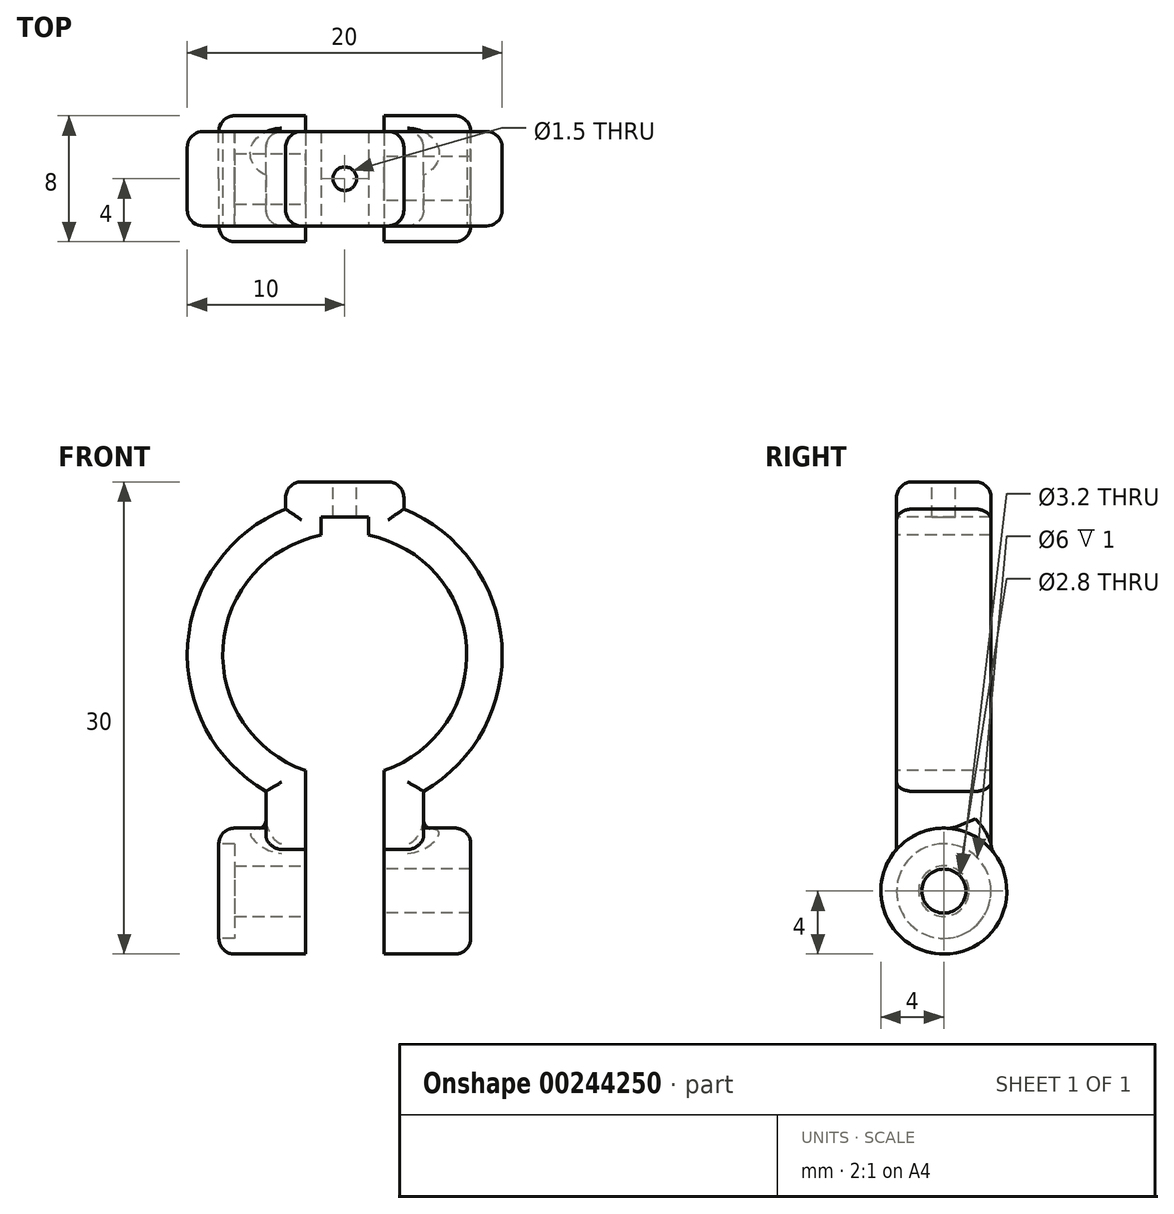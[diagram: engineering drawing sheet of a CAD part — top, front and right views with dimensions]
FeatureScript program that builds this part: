
annotation { "Feature Type Name" : "Feature", "Feature Type Description" : "" }
export const myFeature = defineFeature(function(context is Context, id is Id, definition is map)
    precondition{}
    {
        {
            var Q0;
            Q0=qCreatedBy(makeId("Front.planeOp"),FACE);
            var sketch = newSketch(context, id + "F0", { "sketchPlane" : qUnion([Q0])});
            skCircle(sketch, "E0", {"center": v(0, 0) * mm, "radius": 10 * mm});
            skSolve(sketch);
        }
        {
            var Q0;
            Q0=qSketchRegion(id+"F0",true);
            extrude(context, id + "F1", {"entities" : qUnion([Q0]), "depth" : 5 * mm, "hasSecondDirection" : true, "secondDirectionOppositeDirection" : true, "secondDirectionDepth" : 1 * mm});
        }
        {
            var Q0;
            Q0=makeQuery(id+"F1.opExtrude","CAP_FACE",FACE,{"disambiguationData":[OSD([sQuery(id+"F0.wireOp",EDGE,"E0")])],"isStart":false});
            var sketch = newSketch(context, id + "F2", { "sketchPlane" : qUnion([Q0])});
            skCircle(sketch, "E1", {"center": v(0, 0) * mm, "radius": 7.75 * mm});
            skSolve(sketch);
        }
        {
            var Q0;
            Q0=qSketchRegion(id+"F2",true);
            extrude(context, id + "F3", {"entities" : qUnion([Q0]), "operationType" : NewBodyOperationType.REMOVE, "endBound" : BoundingType.THROUGH_ALL, "oppositeDirection" : true, "depth" : 25 * mm});
        }
        {
            var Q0;
            Q0=qCreatedBy(makeId("Right.planeOp"),FACE);
            var sketch = newSketch(context, id + "F4", { "sketchPlane" : qUnion([Q0])});
            skLineSegment(sketch, "E2.0", {"start": v(1, -10) * mm, "end": v(1, 10) * mm, "construction": true});
            skLineSegment(sketch, "E3.0", {"start": v(-5, -10) * mm, "end": v(-5, 10) * mm, "construction": true});
            skLineSegment(sketch, "E4", {"start": v(-5, -10) * mm, "end": v(1, -10) * mm, "construction": true});
            skLineSegment(sketch, "E5", {"start": v(-2, -10) * mm, "end": v(-2, -15) * mm, "construction": true});
            skCircle(sketch, "E6", {"center": v(-2, -15) * mm, "radius": 4 * mm});
            skSolve(sketch);
        }
        {
            var Q0;
            Q0=qSketchRegion(id+"F4",true);
            extrude(context, id + "F5", {"entities" : qUnion([Q0]), "depth" : 8 * mm, "hasSecondDirection" : true, "secondDirectionOppositeDirection" : true, "secondDirectionDepth" : 8 * mm});
        }
        {
            var Q0;
            Q0=qCreatedBy(makeId("Front.planeOp"),FACE);
            var sketch = newSketch(context, id + "F6", { "sketchPlane" : qUnion([Q0])});
            skLineSegment(sketch, "E7", {"start": v(0, 0) * mm, "end": v(0, -7.75) * mm, "construction": true});
            skLineSegment(sketch, "E8.bottom", {"start": v(-5, -7.75) * mm, "end": v(5, -7.75) * mm});
            skLineSegment(sketch, "E8.top", {"start": v(-5, -15) * mm, "end": v(5, -15) * mm});
            skLineSegment(sketch, "E8.left", {"start": v(-5, -7.75) * mm, "end": v(-5, -15) * mm});
            skLineSegment(sketch, "E8.right", {"start": v(5, -7.75) * mm, "end": v(5, -15) * mm});
            skLineSegment(sketch, "E9.0", {"start": v(-8, -11) * mm, "end": v(-8, -19) * mm, "construction": true});
            skLineSegment(sketch, "E10", {"start": v(-8, -15) * mm, "end": v(-5, -15) * mm, "construction": true});
            skSolve(sketch);
        }
        {
            var Q0;
            Q0=qSketchRegion(id+"F6",true);
            extrude(context, id + "F7", {"entities" : qUnion([Q0]), "operationType" : NewBodyOperationType.ADD, "depth" : 5 * mm, "hasSecondDirection" : true, "secondDirectionOppositeDirection" : true, "secondDirectionDepth" : 1 * mm});
        }
        {
            var Q0;
            Q0=qCreatedBy(makeId("Front.planeOp"),FACE);
            var sketch = newSketch(context, id + "F8", { "sketchPlane" : qUnion([Q0])});
            skLineSegment(sketch, "E11.bottom", {"start": v(-2.5, 0) * mm, "end": v(2.5, 0) * mm});
            skLineSegment(sketch, "E11.top", {"start": v(-2.5, -25.02) * mm, "end": v(2.5, -25.02) * mm});
            skLineSegment(sketch, "E11.left", {"start": v(-2.5, 0) * mm, "end": v(-2.5, -25.02) * mm});
            skLineSegment(sketch, "E11.right", {"start": v(2.5, 0) * mm, "end": v(2.5, -25.02) * mm});
            skSolve(sketch);
        }
        {
            var Q0;
            Q0=qSketchRegion(id+"F8",true);
            extrude(context, id + "F9", {"entities" : qUnion([Q0]), "operationType" : NewBodyOperationType.REMOVE, "endBound" : BoundingType.THROUGH_ALL, "oppositeDirection" : true, "depth" : 25 * mm, "hasSecondDirection" : true, "secondDirectionBound" : SecondDirectionBoundingType.THROUGH_ALL, "secondDirectionOppositeDirection" : false, "secondDirectionDepth" : 25 * mm});
        }
        {
            var Q0;
            Q0=qCreatedBy(makeId("Right.planeOp"),FACE);
            var sketch = newSketch(context, id + "F10", { "sketchPlane" : qUnion([Q0])});
            skCircle(sketch, "E12.0", {"center": v(-2, -15) * mm, "radius": 4 * mm, "construction": true});
            skCircle(sketch, "E13", {"center": v(-2, -15) * mm, "radius": 1.6 * mm});
            skSolve(sketch);
        }
        {
            var Q0;
            Q0=qSketchRegion(id+"F10",true);
            extrude(context, id + "F11", {"entities" : qUnion([Q0]), "operationType" : NewBodyOperationType.REMOVE, "endBound" : BoundingType.THROUGH_ALL, "oppositeDirection" : true, "depth" : 25 * mm});
        }
        {
            var Q0;
            Q0=makeQuery(id+"F5.opExtrude","CAP_FACE",FACE,{"disambiguationData":[OSD([sQuery(id+"F4.wireOp",EDGE,"E6")])],"isStart":true});
            var sketch = newSketch(context, id + "F12", { "sketchPlane" : qUnion([Q0])});
            skCircle(sketch, "E14", {"center": v(2, -15) * mm, "radius": 3 * mm});
            skSolve(sketch);
        }
        {
            var Q0;
            Q0=qSketchRegion(id+"F12",true);
            extrude(context, id + "F13", {"entities" : qUnion([Q0]), "operationType" : NewBodyOperationType.REMOVE, "oppositeDirection" : true, "depth" : 1 * mm});
        }
        {
            var Q0;
            Q0=qCreatedBy(makeId("Right.planeOp"),FACE);
            var sketch = newSketch(context, id + "F14", { "sketchPlane" : qUnion([Q0])});
            skCircle(sketch, "E15.0", {"center": v(-2, -15) * mm, "radius": 4 * mm, "construction": true});
            skCircle(sketch, "E16", {"center": v(-2, -15) * mm, "radius": 1.4 * mm});
            skSolve(sketch);
        }
        {
            var Q0;
            Q0=qSketchRegion(id+"F14",true);
            extrude(context, id + "F15", {"entities" : qUnion([Q0]), "operationType" : NewBodyOperationType.REMOVE, "endBound" : BoundingType.THROUGH_ALL, "depth" : 25 * mm});
        }
        {
            var Q0;
            Q0=makeQuery(id+"F7.boolean.opBoolean","MERGE",FACE,{"derivedFrom":[makeQuery(id+"F1.opExtrude","CAP_FACE",FACE,{"disambiguationData":[OSD([sQuery(id+"F0.wireOp",EDGE,"E0")])],"isStart":false}),makeQuery(id+"F7.opExtrude","CAP_FACE",FACE,{"disambiguationData":[OSD([sQuery(id+"F6.wireOp",EDGE,"E8.bottom"),sQuery(id+"F6.wireOp",EDGE,"E8.top"),sQuery(id+"F6.wireOp",EDGE,"E8.left"),sQuery(id+"F6.wireOp",EDGE,"E8.right")])],"isStart":false})]});
            var sketch = newSketch(context, id + "F16", { "sketchPlane" : qUnion([Q0])});
            skLineSegment(sketch, "E17", {"start": v(0, 0) * mm, "end": v(0, 7.75) * mm, "construction": true});
            skLineSegment(sketch, "E18.bottom", {"start": v(1.5, 8.75) * mm, "end": v(-1.5, 8.75) * mm});
            skLineSegment(sketch, "E18.top", {"start": v(1.5, 6.75) * mm, "end": v(-1.5, 6.75) * mm});
            skLineSegment(sketch, "E18.left", {"start": v(1.5, 8.75) * mm, "end": v(1.5, 6.75) * mm});
            skLineSegment(sketch, "E18.right", {"start": v(-1.5, 8.75) * mm, "end": v(-1.5, 6.75) * mm});
            skPoint(sketch, "E18.middle", {"position": v(0, 7.75) * mm});
            skSolve(sketch);
        }
        {
            var Q0;
            Q0=qSketchRegion(id+"F16",true);
            extrude(context, id + "F17", {"entities" : qUnion([Q0]), "operationType" : NewBodyOperationType.REMOVE, "endBound" : BoundingType.THROUGH_ALL, "oppositeDirection" : true, "depth" : 25 * mm});
        }
        {
            var Q0;
            Q0=makeQuery(id+"F7.boolean.opBoolean","MERGE",FACE,{"derivedFrom":[makeQuery(id+"F1.opExtrude","CAP_FACE",FACE,{"disambiguationData":[OSD([sQuery(id+"F0.wireOp",EDGE,"E0")])],"isStart":false}),makeQuery(id+"F7.opExtrude","CAP_FACE",FACE,{"disambiguationData":[OSD([sQuery(id+"F6.wireOp",EDGE,"E8.bottom"),sQuery(id+"F6.wireOp",EDGE,"E8.top"),sQuery(id+"F6.wireOp",EDGE,"E8.left"),sQuery(id+"F6.wireOp",EDGE,"E8.right")])],"isStart":false})]});
            var sketch = newSketch(context, id + "F18", { "sketchPlane" : qUnion([Q0])});
            skLineSegment(sketch, "E19.0", {"start": v(0, 0) * mm, "end": v(0, 7.75) * mm, "construction": true});
            skLineSegment(sketch, "E19.1", {"start": v(1.5, 8.75) * mm, "end": v(-1.5, 8.75) * mm, "construction": true});
            skLineSegment(sketch, "E19.2", {"start": v(1.5, 6.75) * mm, "end": v(-1.5, 6.75) * mm, "construction": true});
            skLineSegment(sketch, "E19.3", {"start": v(1.5, 8.75) * mm, "end": v(1.5, 6.75) * mm, "construction": true});
            skLineSegment(sketch, "E19.4", {"start": v(-1.5, 8.75) * mm, "end": v(-1.5, 6.75) * mm, "construction": true});
            skPoint(sketch, "E19.5", {"position": v(0, 7.75) * mm});
            skLineSegment(sketch, "E20.0", {"start": v(-3.75, 11) * mm, "end": v(-3.75, 6.75) * mm});
            skLineSegment(sketch, "E20.1", {"start": v(3.75, 11) * mm, "end": v(-3.75, 11) * mm});
            skLineSegment(sketch, "E20.2", {"start": v(3.75, 11) * mm, "end": v(3.75, 6.75) * mm});
            skArc(sketch, "E21.0", {"start": v(-1.5, 7.6) * mm, "mid": v(-2.66, 7.28) * mm, "end": v(-3.75, 6.78) * mm});
            skArc(sketch, "E22.0", {"start": v(3.75, 6.78) * mm, "mid": v(2.66, 7.28) * mm, "end": v(1.5, 7.6) * mm});
            skPoint(sketch, "E23.orphan", {"position": v(-2.5, -7.34) * mm});
            skPoint(sketch, "E24.orphan", {"position": v(2.5, -7.34) * mm});
            skLineSegment(sketch, "E25", {"start": v(-1.5, 7.6) * mm, "end": v(-1.5, 8.75) * mm});
            skLineSegment(sketch, "E26", {"start": v(1.5, 8.75) * mm, "end": v(1.5, 7.6) * mm});
            skLineSegment(sketch, "E27", {"start": v(-1.5, 8.75) * mm, "end": v(1.5, 8.75) * mm});
            skSolve(sketch);
        }
        {
            var Q0;
            Q0=qSketchRegion(id+"F18",true);
            var Q1;
            Q1=makeQuery(id+"F7.boolean.opBoolean","MERGE",FACE,{"derivedFrom":[makeQuery(id+"F1.opExtrude","CAP_FACE",FACE,{"disambiguationData":[OSD([sQuery(id+"F0.wireOp",EDGE,"E0")])],"isStart":true}),makeQuery(id+"F7.opExtrude","CAP_FACE",FACE,{"disambiguationData":[OSD([sQuery(id+"F6.wireOp",EDGE,"E8.bottom"),sQuery(id+"F6.wireOp",EDGE,"E8.top"),sQuery(id+"F6.wireOp",EDGE,"E8.left"),sQuery(id+"F6.wireOp",EDGE,"E8.right")])],"isStart":true})]});
            extrude(context, id + "F19", {"entities" : qUnion([Q0]), "operationType" : NewBodyOperationType.ADD, "endBound" : BoundingType.UP_TO_SURFACE, "oppositeDirection" : true, "endBoundEntityFace" : qUnion([Q1]), "depth" : 25 * mm});
        }
        {
            var Q0;
            Q0=makeQuery(id+"F19.opExtrude","SWEPT_FACE",FACE,{"disambiguationData":[OSD([sQuery(id+"F18.wireOp",EDGE,"E20.1")])]});
            var sketch = newSketch(context, id + "F20", { "sketchPlane" : qUnion([Q0])});
            skLineSegment(sketch, "E28", {"start": v(-3.75, 1) * mm, "end": v(3.75, -5) * mm, "construction": true});
            skCircle(sketch, "E29", {"center": v(0, -2) * mm, "radius": 0.75 * mm});
            skSolve(sketch);
        }
        {
            var Q0;
            Q0=qSketchRegion(id+"F20",true);
            extrude(context, id + "F21", {"entities" : qUnion([Q0]), "operationType" : NewBodyOperationType.REMOVE, "endBound" : BoundingType.UP_TO_NEXT, "oppositeDirection" : true, "depth" : 25 * mm});
        }
        {
            var Q0;
            {var subQ0=sQuery(id+"F6.wireOp",EDGE,"E8.right");var subQ2=sQuery(id+"F0.wireOp",EDGE,"E0");Q0=makeQuery(id+"F19.boolean.opBoolean","SPLIT",EDGE,{"disambiguationData":[TD([makeQuery(id+"F7.opExtrude","SWEPT_FACE",FACE,{"disambiguationData":[OSD([subQ0])]})])],"derivedFrom":makeQuery(id+"F1.opExtrude","CAP_EDGE",EDGE,{"disambiguationData":[OSD([subQ2])],"isStart":false})});}
            var Q1;
            Q1=makeQuery(id+"F19.opExtrude","CAP_EDGE",EDGE,{"disambiguationData":[OSD([sQuery(id+"F18.wireOp",EDGE,"E20.2")])],"isStart":true});
            var Q2;
            Q2=makeQuery(id+"F19.opExtrude","CAP_EDGE",EDGE,{"disambiguationData":[OSD([sQuery(id+"F18.wireOp",EDGE,"E20.1")])],"isStart":true});
            var Q3;
            Q3=makeQuery(id+"F19.opExtrude","CAP_EDGE",EDGE,{"disambiguationData":[OSD([sQuery(id+"F18.wireOp",EDGE,"E20.0")])],"isStart":true});
            var Q4;
            {var subQ0=sQuery(id+"F6.wireOp",EDGE,"E8.left");var subQ1=sQuery(id+"F0.wireOp",EDGE,"E0");Q4=makeQuery(id+"F19.boolean.opBoolean","SPLIT",EDGE,{"disambiguationData":[TD([makeQuery(id+"F7.opExtrude","SWEPT_FACE",FACE,{"disambiguationData":[OSD([subQ0])]})])],"derivedFrom":makeQuery(id+"F1.opExtrude","CAP_EDGE",EDGE,{"disambiguationData":[OSD([subQ1])],"isStart":false})});}
            var Q5;
            Q5=makeQuery(id+"F7.opExtrude","CAP_EDGE",EDGE,{"disambiguationData":[OSD([sQuery(id+"F6.wireOp",EDGE,"E8.left")])],"isStart":false});
            var Q6;
            Q6=makeQuery(id+"F7.opExtrude","CAP_EDGE",EDGE,{"disambiguationData":[OSD([sQuery(id+"F6.wireOp",EDGE,"E8.right")])],"isStart":false});
            var Q7;
            {var subQ0=sQuery(id+"F6.wireOp",EDGE,"E8.right");var subQ1=sQuery(id+"F0.wireOp",EDGE,"E0");Q7=makeQuery(id+"F19.boolean.opBoolean","SPLIT",EDGE,{"disambiguationData":[TD([makeQuery(id+"F7.opExtrude","SWEPT_FACE",FACE,{"disambiguationData":[OSD([subQ0])]})])],"derivedFrom":makeQuery(id+"F1.opExtrude","CAP_EDGE",EDGE,{"disambiguationData":[OSD([subQ1])],"isStart":true})});}
            var Q8;
            Q8=makeQuery(id+"F19.opExtrude","CAP_EDGE",EDGE,{"disambiguationData":[OSD([sQuery(id+"F18.wireOp",EDGE,"E20.2")])],"isStart":false});
            var Q9;
            Q9=makeQuery(id+"F19.opExtrude","CAP_EDGE",EDGE,{"disambiguationData":[OSD([sQuery(id+"F18.wireOp",EDGE,"E20.1")])],"isStart":false});
            var Q10;
            Q10=makeQuery(id+"F19.opExtrude","CAP_EDGE",EDGE,{"disambiguationData":[OSD([sQuery(id+"F18.wireOp",EDGE,"E20.0")])],"isStart":false});
            var Q11;
            {var subQ0=sQuery(id+"F6.wireOp",EDGE,"E8.left");var subQ1=sQuery(id+"F0.wireOp",EDGE,"E0");Q11=makeQuery(id+"F19.boolean.opBoolean","SPLIT",EDGE,{"disambiguationData":[TD([makeQuery(id+"F7.opExtrude","SWEPT_FACE",FACE,{"disambiguationData":[OSD([subQ0])]})])],"derivedFrom":makeQuery(id+"F1.opExtrude","CAP_EDGE",EDGE,{"disambiguationData":[OSD([subQ1])],"isStart":true})});}
            var Q12;
            Q12=makeQuery(id+"F7.opExtrude","CAP_EDGE",EDGE,{"disambiguationData":[OSD([sQuery(id+"F6.wireOp",EDGE,"E8.left")])],"isStart":true});
            var Q13;
            Q13=makeQuery(id+"F7.opExtrude","CAP_EDGE",EDGE,{"disambiguationData":[OSD([sQuery(id+"F6.wireOp",EDGE,"E8.right")])],"isStart":true});
            var Q14;
            {var subQ0=sQuery(id+"F6.wireOp",EDGE,"E8.right");var subQ1=makeQuery(id+"F7.opExtrude","CAP_FACE",FACE,{"disambiguationData":[OSD([sQuery(id+"F6.wireOp",EDGE,"E8.bottom"),sQuery(id+"F6.wireOp",EDGE,"E8.top"),sQuery(id+"F6.wireOp",EDGE,"E8.left"),subQ0])],"isStart":true});var subQ2=makeQuery(id+"F5.opExtrude","SWEPT_FACE",FACE,{"disambiguationData":[OSD([sQuery(id+"F4.wireOp",EDGE,"E6")])]});Q14=makeQuery(id+"F9.boolean.opBoolean","SPLIT",EDGE,{"disambiguationData":[TD([makeQuery(id+"F7.opExtrude","SWEPT_FACE",FACE,{"disambiguationData":[OSD([subQ0])]})])],"derivedFrom":makeQuery(id+"F7.boolean.opBoolean","INTERSECT",EDGE,{"derivedFrom":[subQ2,subQ1]})});}
            var Q15;
            {var subQ0=sQuery(id+"F6.wireOp",EDGE,"E8.left");var subQ1=makeQuery(id+"F7.opExtrude","CAP_FACE",FACE,{"disambiguationData":[OSD([sQuery(id+"F6.wireOp",EDGE,"E8.bottom"),sQuery(id+"F6.wireOp",EDGE,"E8.top"),subQ0,sQuery(id+"F6.wireOp",EDGE,"E8.right")])],"isStart":true});var subQ2=makeQuery(id+"F5.opExtrude","SWEPT_FACE",FACE,{"disambiguationData":[OSD([sQuery(id+"F4.wireOp",EDGE,"E6")])]});Q15=makeQuery(id+"F9.boolean.opBoolean","SPLIT",EDGE,{"disambiguationData":[TD([makeQuery(id+"F7.opExtrude","SWEPT_FACE",FACE,{"disambiguationData":[OSD([subQ0])]})])],"derivedFrom":makeQuery(id+"F7.boolean.opBoolean","INTERSECT",EDGE,{"derivedFrom":[subQ2,subQ1]})});}
            var Q16;
            Q16=makeQuery(id+"F19.opExtrude","SWEPT_EDGE",EDGE,{"disambiguationData":[OSD([sQuery(id+"F18.wireOp",EDGE,"E20.0"),sQuery(id+"F18.wireOp",EDGE,"E20.1")])]});
            var Q17;
            Q17=makeQuery(id+"F19.opExtrude","SWEPT_EDGE",EDGE,{"disambiguationData":[OSD([sQuery(id+"F18.wireOp",EDGE,"E20.1"),sQuery(id+"F18.wireOp",EDGE,"E20.2")])]});
            var Q18;
            Q18=makeQuery(id+"F5.opExtrude","CAP_EDGE",EDGE,{"disambiguationData":[OSD([sQuery(id+"F4.wireOp",EDGE,"E6")])],"isStart":true});
            var Q19;
            Q19=makeQuery(id+"F5.opExtrude","CAP_EDGE",EDGE,{"disambiguationData":[OSD([sQuery(id+"F4.wireOp",EDGE,"E6")])],"isStart":false});
            fillet(context, id + "F22", {"entities" : qUnion([Q0, Q1, Q2, Q3, Q4, Q5, Q6, Q7, Q8, Q9, Q10, Q11, Q12, Q13, Q14, Q15, Q16, Q17, Q18, Q19]), "radius" : 1 * mm, "tangentPropagation" : true, "allowEdgeOverflow" : false});
        }
    });
